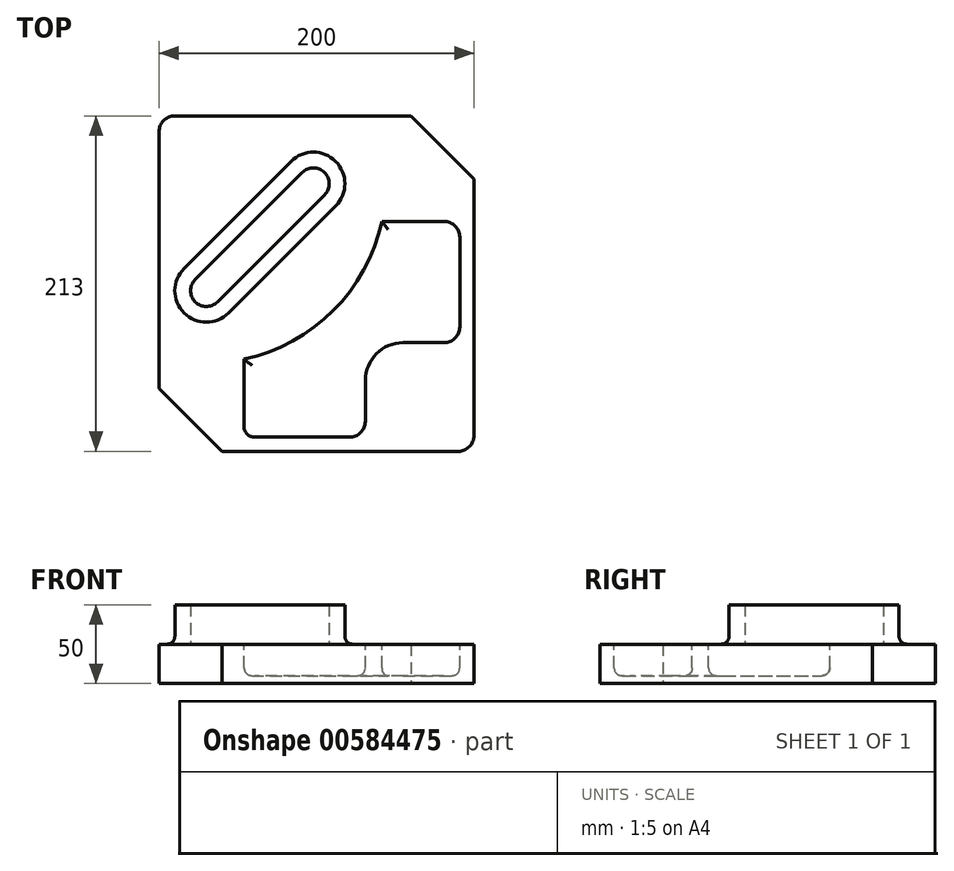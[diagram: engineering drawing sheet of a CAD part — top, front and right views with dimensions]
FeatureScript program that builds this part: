
annotation { "Feature Type Name" : "Feature", "Feature Type Description" : "" }
export const myFeature = defineFeature(function(context is Context, id is Id, definition is map)
    precondition{}
    {
        {
            var Q0;
            Q0=qCreatedBy(makeId("Top.planeOp"),FACE);
            var sketch = newSketch(context, id + "F0", { "sketchPlane" : qUnion([Q0])});
            skLineSegment(sketch, "E0.bottom", {"start": v(100, -106.5) * mm, "end": v(-60, -106.5) * mm});
            skLineSegment(sketch, "E0.top", {"start": v(60, 106.5) * mm, "end": v(-100, 106.5) * mm});
            skLineSegment(sketch, "E0.left", {"start": v(100, -106.5) * mm, "end": v(100, 66.5) * mm});
            skLineSegment(sketch, "E0.right", {"start": v(-100, -66.5) * mm, "end": v(-100, 106.5) * mm});
            skPoint(sketch, "E0.middle", {"position": v(0, 0) * mm});
            skLineSegment(sketch, "E1", {"start": v(60, 106.5) * mm, "end": v(100, 66.5) * mm});
            skLineSegment(sketch, "E2", {"start": v(-100, -66.5) * mm, "end": v(-60, -106.5) * mm});
            skPoint(sketch, "E3.orphan", {"position": v(100, 106.5) * mm});
            skPoint(sketch, "E4.orphan", {"position": v(-100, -106.5) * mm});
            skSolve(sketch);
        }
        {
            var Q0;
            Q0=makeQuery(id+"F0.imprint","IMPRINT",FACE,{"disambiguationData":[TD([[makeQuery(id+"F0.imprint","IMPRINT",EDGE,{"derivedFrom":sQuery(id+"F0.wireOp",EDGE,"E0.bottom")}),-1.0]])]});
            extrude(context, id + "F1", {"entities" : qUnion([Q0]), "depth" : 25 * mm, "offsetDistance" : 25 * mm});
        }
        {
            var Q0;
            Q0=makeQuery(id+"F1.opExtrude","CAP_FACE",FACE,{"disambiguationData":[OSD([sQuery(id+"F0.wireOp",EDGE,"E0.bottom"),sQuery(id+"F0.wireOp",EDGE,"E0.top"),sQuery(id+"F0.wireOp",EDGE,"E0.left"),sQuery(id+"F0.wireOp",EDGE,"E0.right"),sQuery(id+"F0.wireOp",EDGE,"E1"),sQuery(id+"F0.wireOp",EDGE,"E2")])],"isStart":false});
            var sketch = newSketch(context, id + "F2", { "sketchPlane" : qUnion([Q0])});
            skLineSegment(sketch, "E5", {"start": v(55, -37.5) * mm, "end": v(81, -37.5) * mm});
            skArc(sketch, "E6", {"start": v(81, -37.5) * mm, "mid": v(88.07, -34.57) * mm, "end": v(91, -27.5) * mm});
            skLineSegment(sketch, "E7", {"start": v(91, -27.5) * mm, "end": v(91, 29.5) * mm});
            skArc(sketch, "E8", {"start": v(91, 29.5) * mm, "mid": v(88.07, 36.57) * mm, "end": v(81, 39.5) * mm});
            skLineSegment(sketch, "E9", {"start": v(81, 39.5) * mm, "end": v(41.45, 39.5) * mm});
            skArc(sketch, "E10", {"start": v(55, -37.5) * mm, "mid": v(38.03, -44.53) * mm, "end": v(31, -61.5) * mm});
            skLineSegment(sketch, "E11", {"start": v(31, -61.5) * mm, "end": v(31, -87.5) * mm});
            skArc(sketch, "E12", {"start": v(31, -87.5) * mm, "mid": v(28.07, -94.57) * mm, "end": v(21, -97.5) * mm});
            skLineSegment(sketch, "E13", {"start": v(21, -97.5) * mm, "end": v(-39.48, -97.5) * mm});
            skArc(sketch, "E14", {"start": v(-39.48, -97.5) * mm, "mid": v(-44.09, -95.59) * mm, "end": v(-46, -90.98) * mm});
            skLineSegment(sketch, "E15", {"start": v(-46, -90.98) * mm, "end": v(-46, -47.95) * mm});
            skArc(sketch, "E16", {"start": v(-46, -47.95) * mm, "mid": v(10.61, -17.11) * mm, "end": v(41.45, 39.5) * mm});
            skSolve(sketch);
        }
        {
            var Q0;
            Q0=makeQuery(id+"F2.imprint","IMPRINT",FACE,{"disambiguationData":[TD([[makeQuery(id+"F2.imprint","IMPRINT",EDGE,{"derivedFrom":sQuery(id+"F2.wireOp",EDGE,"E5")}),1.0]])]});
            extrude(context, id + "F3", {"entities" : qUnion([Q0]), "operationType" : NewBodyOperationType.REMOVE, "oppositeDirection" : true, "depth" : 20 * mm, "offsetDistance" : 25 * mm});
        }
        {
            var Q0;
            Q0=makeQuery(id+"F1.opExtrude","CAP_FACE",FACE,{"disambiguationData":[OSD([sQuery(id+"F0.wireOp",EDGE,"E0.bottom"),sQuery(id+"F0.wireOp",EDGE,"E0.top"),sQuery(id+"F0.wireOp",EDGE,"E0.left"),sQuery(id+"F0.wireOp",EDGE,"E0.right"),sQuery(id+"F0.wireOp",EDGE,"E1"),sQuery(id+"F0.wireOp",EDGE,"E2")])],"isStart":false});
            var sketch = newSketch(context, id + "F4", { "sketchPlane" : qUnion([Q0])});
            skArc(sketch, "E17", {"start": v(5.07, 56.43) * mm, "mid": v(5.07, 70.57) * mm, "end": v(-9.07, 70.57) * mm});
            skArc(sketch, "E18", {"start": v(-77.07, 2.57) * mm, "mid": v(-77.07, -11.57) * mm, "end": v(-62.93, -11.57) * mm});
            skLineSegment(sketch, "E19", {"start": v(-77.07, 2.57) * mm, "end": v(-9.07, 70.57) * mm});
            skLineSegment(sketch, "E20", {"start": v(-62.93, -11.57) * mm, "end": v(5.07, 56.43) * mm});
            skArc(sketch, "E21", {"start": v(-84.14, 9.64) * mm, "mid": v(-84.14, -18.64) * mm, "end": v(-55.86, -18.64) * mm});
            skArc(sketch, "E22", {"start": v(12.14, 49.36) * mm, "mid": v(12.14, 77.64) * mm, "end": v(-16.14, 77.64) * mm});
            skLineSegment(sketch, "E23", {"start": v(-84.14, 9.64) * mm, "end": v(-16.14, 77.64) * mm});
            skLineSegment(sketch, "E24", {"start": v(12.14, 49.36) * mm, "end": v(-55.86, -18.64) * mm});
            skSolve(sketch);
        }
        {
            var Q0;
            Q0=makeQuery(id+"F4.imprint","IMPRINT",FACE,{"disambiguationData":[TD([[makeQuery(id+"F4.imprint","IMPRINT",EDGE,{"derivedFrom":sQuery(id+"F4.wireOp",EDGE,"E17")}),-1.0]])]});
            extrude(context, id + "F5", {"entities" : qUnion([Q0]), "operationType" : NewBodyOperationType.ADD, "depth" : 25 * mm, "offsetDistance" : 25 * mm});
        }
        {
            var Q0;
            Q0=makeQuery(id+"F1.opExtrude","SWEPT_EDGE",EDGE,{"disambiguationData":[OSD([sQuery(id+"F0.wireOp",EDGE,"E0.bottom"),sQuery(id+"F0.wireOp",EDGE,"E0.left")])]});
            var Q1;
            Q1=makeQuery(id+"F1.opExtrude","SWEPT_EDGE",EDGE,{"disambiguationData":[OSD([sQuery(id+"F0.wireOp",EDGE,"E0.top"),sQuery(id+"F0.wireOp",EDGE,"E0.right")])]});
            fillet(context, id + "F6", {"entities" : qUnion([Q0, Q1]), "radius" : 10 * mm, "tangentPropagation" : true, "allowEdgeOverflow" : false});
        }
        {
            var Q0;
            Q0=makeQuery(id+"F5.opExtrude","CAP_EDGE",EDGE,{"disambiguationData":[OSD([sQuery(id+"F4.wireOp",EDGE,"E24")])],"isStart":true});
            var Q1;
            Q1=makeQuery(id+"F3.boolean.opBoolean","COPY",EDGE,{"derivedFrom":makeQuery(id+"F3.opExtrude","CAP_EDGE",EDGE,{"disambiguationData":[OSD([sQuery(id+"F2.wireOp",EDGE,"E16")])],"isStart":false})});
            var Q2;
            Q2=makeQuery(id+"F3.boolean.opBoolean","COPY",EDGE,{"derivedFrom":makeQuery(id+"F3.opExtrude","CAP_EDGE",EDGE,{"disambiguationData":[OSD([sQuery(id+"F2.wireOp",EDGE,"E9")])],"isStart":false})});
            var Q3;
            Q3=makeQuery(id+"F3.boolean.opBoolean","COPY",EDGE,{"derivedFrom":makeQuery(id+"F3.opExtrude","CAP_EDGE",EDGE,{"disambiguationData":[OSD([sQuery(id+"F2.wireOp",EDGE,"E9")])],"isStart":true})});
            var Q4;
            Q4=makeQuery(id+"F3.boolean.opBoolean","COPY",EDGE,{"derivedFrom":makeQuery(id+"F3.opExtrude","CAP_EDGE",EDGE,{"disambiguationData":[OSD([sQuery(id+"F2.wireOp",EDGE,"E16")])],"isStart":true})});
            fillet(context, id + "F7", {"entities" : qUnion([Q0, Q1, Q2, Q3, Q4]), "radius" : 5 * mm, "tangentPropagation" : true, "allowEdgeOverflow" : false});
        }
    });
